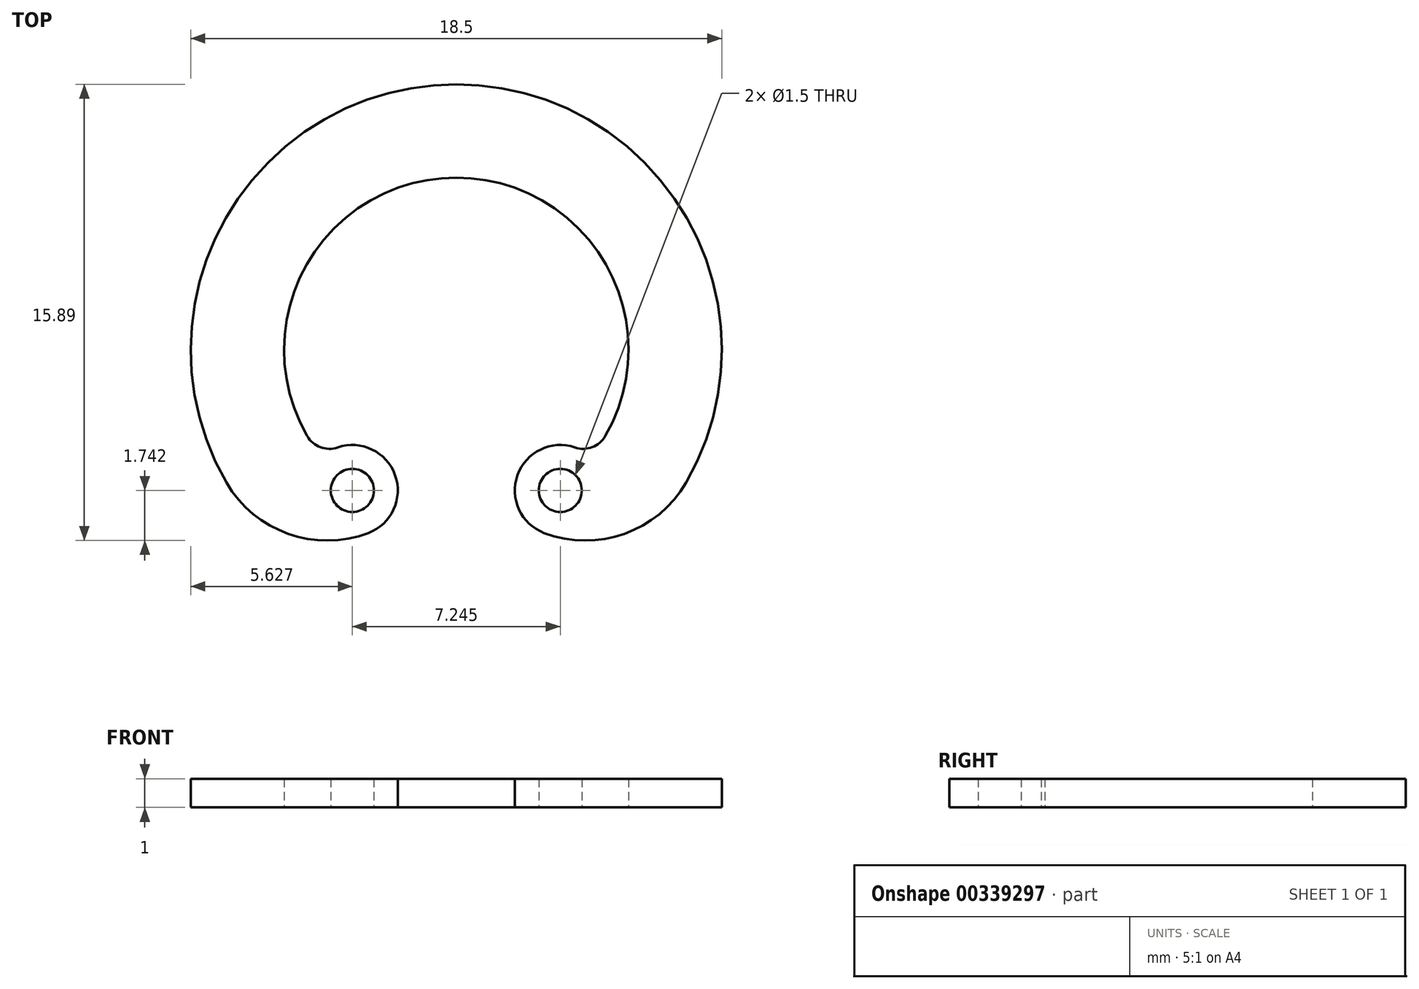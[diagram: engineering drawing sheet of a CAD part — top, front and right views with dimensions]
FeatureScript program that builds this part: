
annotation { "Feature Type Name" : "Feature", "Feature Type Description" : "" }
export const myFeature = defineFeature(function(context is Context, id is Id, definition is map)
    precondition{}
    {
        {
            var Q0;
            Q0=qCreatedBy(makeId("Top.planeOp"),FACE);
            var sketch = newSketch(context, id + "F0", { "sketchPlane" : qUnion([Q0])});
            skCircle(sketch, "E0", {"center": v(0, 0) * mm, "radius": 9.25 * mm, "construction": true});
            skCircle(sketch, "E1", {"center": v(0, 0) * mm, "radius": 6 * mm, "construction": true});
            skLineSegment(sketch, "E2", {"start": v(0, 6) * mm, "end": v(15.31, 6) * mm, "construction": true});
            skLineSegment(sketch, "E3", {"start": v(0, 6) * mm, "end": v(-12.46, 6) * mm, "construction": true});
            skLineSegment(sketch, "E4", {"start": v(0, 9.25) * mm, "end": v(12.89, 9.25) * mm, "construction": true});
            skLineSegment(sketch, "E5", {"start": v(0, 9.25) * mm, "end": v(-12.37, 9.25) * mm, "construction": true});
            skCircle(sketch, "E6", {"center": v(0, 0) * mm, "radius": 4.5 * mm, "construction": true});
            skLineSegment(sketch, "E7", {"start": v(0, 0) * mm, "end": v(-13.02, -7.52) * mm, "construction": true});
            skLineSegment(sketch, "E8.MirrorCS", {"start": v(0, 0) * mm, "end": v(13.02, -7.52) * mm, "construction": true});
            skArc(sketch, "E9", {"start": v(5.2, -3) * mm, "mid": v(0, 6) * mm, "end": v(-5.2, -3) * mm});
            skArc(sketch, "E10", {"start": v(8.01, -4.63) * mm, "mid": v(0, 9.25) * mm, "end": v(-8.01, -4.63) * mm});
            skArc(sketch, "E11", {"start": v(-5.2, -3) * mm, "mid": v(-4.74, -3.4) * mm, "end": v(-4.13, -3.4) * mm});
            skArc(sketch, "E12", {"start": v(-4.13, -3.4) * mm, "mid": v(-2.13, -4.36) * mm, "end": v(-3.06, -6.38) * mm});
            skArc(sketch, "E13", {"start": v(-3.06, -6.38) * mm, "mid": v(-5.86, -6.4) * mm, "end": v(-8.01, -4.63) * mm});
            skCircle(sketch, "E14", {"center": v(-3.62, -4.9) * mm, "radius": 0.75 * mm});
            skArc(sketch, "E15.MirrorCS", {"start": v(4.13, -3.4) * mm, "mid": v(2.13, -4.36) * mm, "end": v(3.06, -6.38) * mm});
            skCircle(sketch, "E16.MirrorC", {"center": v(3.62, -4.9) * mm, "radius": 0.75 * mm});
            skArc(sketch, "E17.MirrorCS", {"start": v(3.06, -6.38) * mm, "mid": v(5.86, -6.4) * mm, "end": v(8.01, -4.63) * mm});
            skArc(sketch, "E18.MirrorCS", {"start": v(5.2, -3) * mm, "mid": v(4.74, -3.4) * mm, "end": v(4.13, -3.4) * mm});
            skSolve(sketch);
        }
        {
            var Q0;
            Q0 = qSketchRegion(id + "F0", true);
            extrude(context, id + "F1", {"entities" : qUnion([Q0]), "depth" : 1 * mm, "offsetDistance" : 25 * mm});
        }
    });
